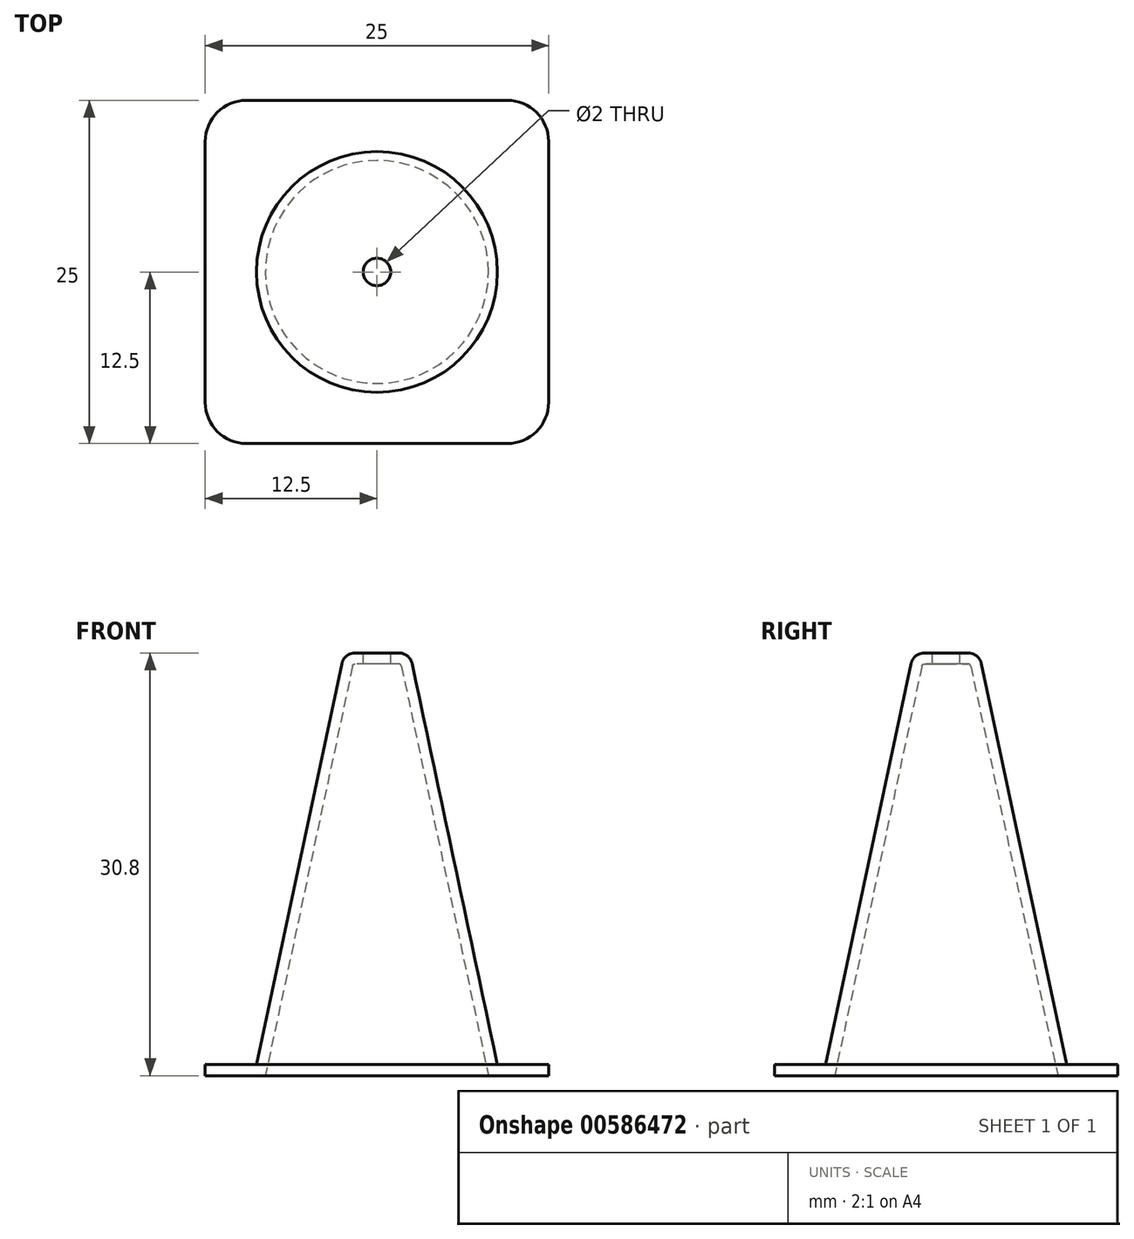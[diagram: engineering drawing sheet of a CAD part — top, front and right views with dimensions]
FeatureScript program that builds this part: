
annotation { "Feature Type Name" : "Feature", "Feature Type Description" : "" }
export const myFeature = defineFeature(function(context is Context, id is Id, definition is map)
    precondition{}
    {
        {
            var Q0;
            Q0=qCreatedBy(makeId("Top.planeOp"),FACE);
            var sketch = newSketch(context, id + "F0", { "sketchPlane" : qUnion([Q0])});
            skLineSegment(sketch, "E0.bottom", {"start": v(12.5, -12.5) * mm, "end": v(-12.5, -12.5) * mm});
            skLineSegment(sketch, "E0.top", {"start": v(12.5, 12.5) * mm, "end": v(-12.5, 12.5) * mm});
            skLineSegment(sketch, "E0.left", {"start": v(12.5, -12.5) * mm, "end": v(12.5, 12.5) * mm});
            skLineSegment(sketch, "E0.right", {"start": v(-12.5, -12.5) * mm, "end": v(-12.5, 12.5) * mm});
            skPoint(sketch, "E0.middle", {"position": v(0, 0) * mm});
            skSolve(sketch);
        }
        {
            var Q0;
            Q0 = qSketchRegion(id + "F0", true);
            extrude(context, id + "F1", {"entities" : qUnion([Q0]), "depth" : 1.2 * mm, "offsetDistance" : 25 * mm});
        }
        {
            var Q0;
            Q0=makeQuery(id+"F1.opExtrude","CAP_FACE",FACE,{"disambiguationData":[OSD([sQuery(id+"F0.wireOp",EDGE,"E0.bottom"),sQuery(id+"F0.wireOp",EDGE,"E0.top"),sQuery(id+"F0.wireOp",EDGE,"E0.left"),sQuery(id+"F0.wireOp",EDGE,"E0.right")])],"isStart":false});
            var sketch = newSketch(context, id + "F2", { "sketchPlane" : qUnion([Q0])});
            skCircle(sketch, "E1", {"center": v(0, 0) * mm, "radius": 8.77 * mm});
            skSolve(sketch);
        }
        {
            var Q0;
            Q0 = qSketchRegion(id + "F2", true);
            extrude(context, id + "F3", {"entities" : qUnion([Q0]), "operationType" : NewBodyOperationType.ADD, "depth" : 30 * mm, "offsetDistance" : 25 * mm, "hasDraft" : true, "draftAngle" : 12 * degree, "draftPullDirection" : true});
        }
        {
            var Q0;
            Q0=makeQuery(id+"F3.opExtrude","CAP_EDGE",EDGE,{"disambiguationData":[OSD([sQuery(id+"F2.wireOp",EDGE,"E1")])],"isStart":false});
            fillet(context, id + "F4", {"entities" : qUnion([Q0]), "radius" : 1 * mm, "tangentPropagation" : true, "allowEdgeOverflow" : false});
        }
        {
            var Q0;
            Q0=makeQuery(id+"F1.opExtrude","SWEPT_EDGE",EDGE,{"disambiguationData":[OSD([sQuery(id+"F0.wireOp",EDGE,"E0.bottom"),sQuery(id+"F0.wireOp",EDGE,"E0.right")])]});
            var Q1;
            Q1=makeQuery(id+"F1.opExtrude","SWEPT_EDGE",EDGE,{"disambiguationData":[OSD([sQuery(id+"F0.wireOp",EDGE,"E0.top"),sQuery(id+"F0.wireOp",EDGE,"E0.right")])]});
            var Q2;
            Q2=makeQuery(id+"F1.opExtrude","SWEPT_EDGE",EDGE,{"disambiguationData":[OSD([sQuery(id+"F0.wireOp",EDGE,"E0.top"),sQuery(id+"F0.wireOp",EDGE,"E0.left")])]});
            var Q3;
            Q3=makeQuery(id+"F1.opExtrude","SWEPT_EDGE",EDGE,{"disambiguationData":[OSD([sQuery(id+"F0.wireOp",EDGE,"E0.bottom"),sQuery(id+"F0.wireOp",EDGE,"E0.left")])]});
            fillet(context, id + "F5", {"entities" : qUnion([Q0, Q1, Q2, Q3]), "radius" : 3 * mm, "tangentPropagation" : true, "allowEdgeOverflow" : false});
        }
        {
            var Q0;
            Q0=makeQuery(id+"F1.opExtrude","CAP_FACE",FACE,{"disambiguationData":[OSD([sQuery(id+"F0.wireOp",EDGE,"E0.bottom"),sQuery(id+"F0.wireOp",EDGE,"E0.top"),sQuery(id+"F0.wireOp",EDGE,"E0.left"),sQuery(id+"F0.wireOp",EDGE,"E0.right")])],"isStart":true});
            shell(context, id + "F6", {"entities" : qUnion([Q0]), "thickness" : .8 * mm});
        }
        {
            var Q0;
            Q0=makeQuery(id+"F1.opExtrude","CAP_FACE",FACE,{"disambiguationData":[OSD([sQuery(id+"F0.wireOp",EDGE,"E0.bottom"),sQuery(id+"F0.wireOp",EDGE,"E0.top"),sQuery(id+"F0.wireOp",EDGE,"E0.left"),sQuery(id+"F0.wireOp",EDGE,"E0.right")])],"isStart":true});
            var Q1;
            Q1=makeQuery(id+"F6.opShell","OFFSET_FACE",FACE,{"disambiguationData":[OSD([sQuery(id+"F0.wireOp",EDGE,"E0.bottom"),sQuery(id+"F0.wireOp",EDGE,"E0.top"),sQuery(id+"F0.wireOp",EDGE,"E0.left"),sQuery(id+"F0.wireOp",EDGE,"E0.right")])]});
            extrude(context, id + "F7", {"entities" : qUnion([Q0]), "operationType" : NewBodyOperationType.REMOVE, "endBound" : BoundingType.UP_TO_SURFACE, "oppositeDirection" : true, "depth" : 25 * mm, "endBoundEntityFace" : qUnion([Q1]), "offsetDistance" : 25 * mm});
        }
        {
            var Q0;
            Q0=makeQuery(id+"F3.opExtrude","CAP_FACE",FACE,{"disambiguationData":[OSD([sQuery(id+"F2.wireOp",EDGE,"E1")])],"isStart":false});
            var sketch = newSketch(context, id + "F8", { "sketchPlane" : qUnion([Q0])});
            skCircle(sketch, "E2", {"center": v(0, 0) * mm, "radius": 1 * mm});
            skSolve(sketch);
        }
        {
            var Q0;
            Q0=makeQuery(id+"F8.imprint","IMPRINT",FACE,{"disambiguationData":[TD([[makeQuery(id+"F8.imprint","IMPRINT",EDGE,{"derivedFrom":sQuery(id+"F8.wireOp",EDGE,"E2")}),1.0]])]});
            extrude(context, id + "F9", {"entities" : qUnion([Q0]), "operationType" : NewBodyOperationType.REMOVE, "endBound" : BoundingType.THROUGH_ALL, "oppositeDirection" : true, "depth" : 25 * mm, "offsetDistance" : 25 * mm});
        }
    });
